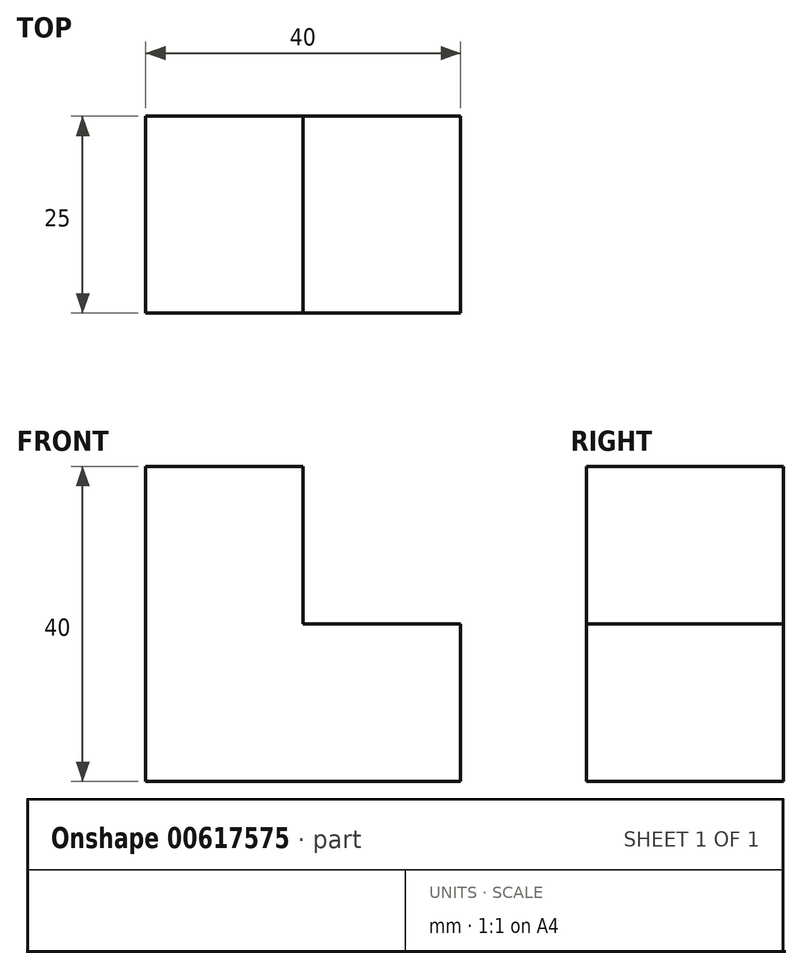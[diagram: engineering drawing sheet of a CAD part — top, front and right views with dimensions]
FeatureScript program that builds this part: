
annotation { "Feature Type Name" : "Feature", "Feature Type Description" : "" }
export const myFeature = defineFeature(function(context is Context, id is Id, definition is map)
    precondition{}
    {
        {
            var Q0;
            Q0=qCreatedBy(makeId("Front.planeOp"),FACE);
            var sketch = newSketch(context, id + "F0", { "sketchPlane" : qUnion([Q0])});
            skLineSegment(sketch, "E0", {"start": v(0, 0) * mm, "end": v(0, -20) * mm});
            skLineSegment(sketch, "E1", {"start": v(0, -20) * mm, "end": v(20, -20) * mm});
            skLineSegment(sketch, "E2", {"start": v(20, -20) * mm, "end": v(20, 0) * mm});
            skLineSegment(sketch, "E3", {"start": v(20, 0) * mm, "end": v(0, 0) * mm});
            skLineSegment(sketch, "E4", {"start": v(-20, 0) * mm, "end": v(-20, -20) * mm});
            skLineSegment(sketch, "E5", {"start": v(-20, -20) * mm, "end": v(0, -20) * mm});
            skLineSegment(sketch, "E6", {"start": v(-20, 20) * mm, "end": v(-20, 0) * mm});
            skLineSegment(sketch, "E7", {"start": v(0, 0) * mm, "end": v(-20, 0) * mm});
            skLineSegment(sketch, "E8", {"start": v(0, 0) * mm, "end": v(0, 20) * mm});
            skLineSegment(sketch, "E9", {"start": v(0, 20) * mm, "end": v(-20, 20) * mm});
            skSolve(sketch);
        }
        {
            var Q0;
            Q0 = qSketchRegion(id + "F0", true);
            extrude(context, id + "F1", {"entities" : qUnion([Q0]), "depth" : 25 * mm, "offsetDistance" : 25 * mm});
        }
    });
